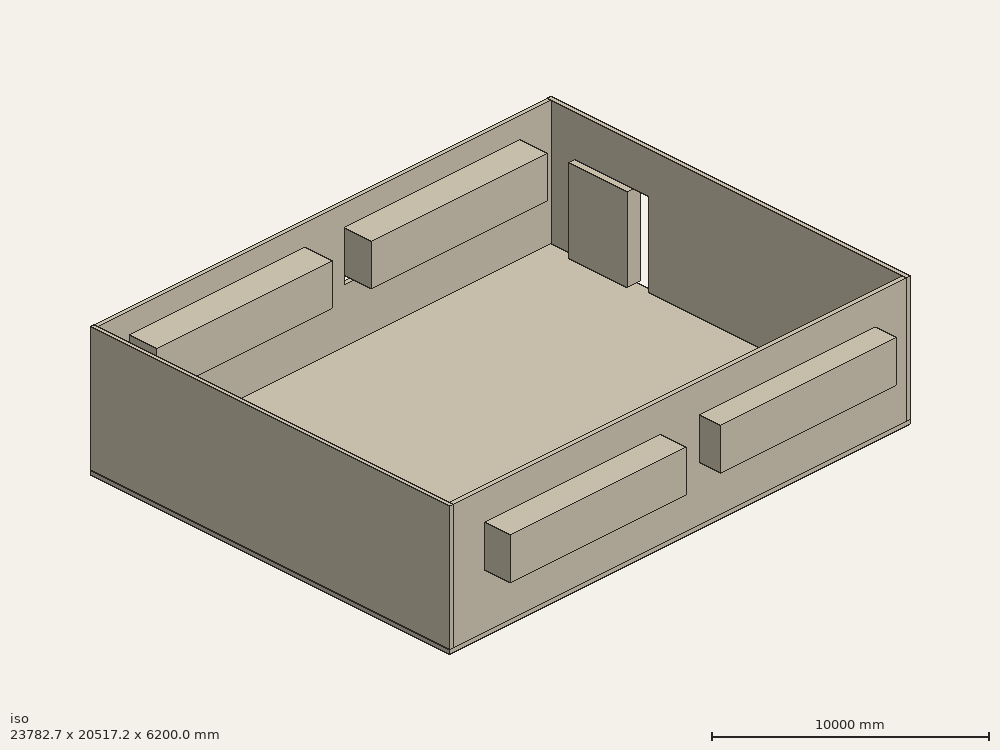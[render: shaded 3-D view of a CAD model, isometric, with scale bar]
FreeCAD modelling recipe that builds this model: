
FCSTD DOCUMENT  (FreeCAD 0.19R)
Label: warehouse
License: All rights reserved
LicenseURL: http://en.wikipedia.org/wiki/All_rights_reserved
objects: App::FeaturePython×14, Part::Box×5, Part::FeaturePython×5, Sketcher::SketchObject×4, App::MaterialObjectPython×2, Part::Part2DObjectPython×1, App::DocumentObjectGroupPython×1, App::DocumentObjectGroup×1, App::GeometryPython×1
note: 16 computed .brp shape members not serialized (recipe doc carries the construction recipe); baked Part::Feature solids carry a one-line shape summary decoded from their .brp

FEATURE [Sketcher::SketchObject] WallTrace002
  FullyConstrained = false
  sketch-geometry (1):
    g0: LineSegment StartX=-1.1328e-12 StartY=18500 StartZ=0 EndX=23200 EndY=18500 EndZ=0
FEATURE [Sketcher::SketchObject] WallTrace
  FullyConstrained = false
  sketch-geometry (1):
    g0: LineSegment StartX=-100 StartY=-200 StartZ=0 EndX=-100 EndY=18200 EndZ=0
FEATURE [Sketcher::SketchObject] WallTrace001
  FullyConstrained = false
  sketch-geometry (1):
    g0: LineSegment StartX=-6.1e-15 StartY=-100 StartZ=0 EndX=23200 EndY=-100 EndZ=0
FEATURE [App::FeaturePython] Dimension001  # Draft dimension (typed FeaturePython)
  Diameter = false
  Dimline = (9000,8000,0)
  Direction = (0,0,0)
  Distance = 23200
  End = (23200,9000,0)
  Normal = (0,0,1)
  Start = (-8.353e-13,9000,0)
FEATURE [App::FeaturePython] Dimension  # Draft dimension (typed FeaturePython)
  Diameter = false
  Dimline = (11900,8900,0)
  Direction = (0,0,0)
  Distance = 18000
  End = (11600,0,0)
  Normal = (0,0,1)
  Start = (11600,18000,0)
FEATURE [Sketcher::SketchObject] WallTrace003
  FullyConstrained = false
  sketch-geometry (1):
    g0: LineSegment StartX=23300 StartY=18600 StartZ=0 EndX=23300 EndY=200 EndZ=0
FEATURE [Part::Box] Cube
  AttacherType = Attacher::AttachEngine3D
  Height = 4000
  Length = 687.6
  Placement = pos=(23582.7,16800,0) rot=(0,0,1;3.14159rad)
  Width = 3000
FEATURE [App::FeaturePython] Dimension002  # Draft dimension (typed FeaturePython)
  Diameter = false
  Dimline = (22729.1,17106.1,0)
  Direction = (0,0,0)
  Distance = 2000
  End = (22682.3,16000,0)
  Normal = (0,0,1)
  Start = (22682.3,18000,0)
FEATURE [App::FeaturePython] Dimension003  # Draft dimension (typed FeaturePython)
  Diameter = false
  Dimline = (23259.5,14201,0)
  Direction = (0,0,0)
  Distance = 3000
  End = (23326.6,13000,0)
  Normal = (0,0,1)
  Start = (23326.6,16000,0)
FEATURE [App::MaterialObjectPython] Material  label="Concrete"  # material (typed FeaturePython)
  Description = A standard C-25 construction concrete
  Material = AuthorAndLicense=Concrete-Generic,CardName=Concrete-Generic,Color=(1.0, 0.7568627450980392, 0.27058823529411763, 1.0),CompressiveStrength=25 MPa,+12 more (map truncated)
  ProductURL = https://en.wikipedia.org/wiki/Concrete
  StandardCode = Masterformat 03 33 13
  Transparency = 0
FEATURE [Part::FeaturePython] Wall003  # Arch/BIM 166 (typed FeaturePython)
  Align = 2
  Area = 0
  Base = -> WallTrace003
  BlockHeight = 0
  BlockLength = 0
  CountBroken = 0
  CountEntire = 0
  Face = 0
  Height = 0
  HorizontalArea = 3680000
  IfcData = attributes={"GlobalId": {"name": "GlobalId", "type": "IfcGloballyUniqueId", "is_enum": false, "enum_values": []}, "Description": {"... (+533 chars omitted),+1 more (map truncated)
  IfcType = 166
  Joint = 0
  Length = 18400
  MakeBlocks = false
  Material = -> Material
  MoveBase = false
  MoveWithHost = false
  Normal = (0,0,1)
  OffsetFirst = 0
  OffsetSecond = 0
  PerimeterLength = 37200
  Placement = pos=(0,-400,0) rot=(0,0,1;0rad)
  PredefinedType = 0
  Subtractions = -> [Cube]
  VerticalArea = 200800000
  Width = 200
FEATURE [Part::FeaturePython] Wall001  # Arch/BIM 166 (typed FeaturePython)
  Align = 2
  Area = 0
  Base = -> WallTrace
  BlockHeight = 0
  BlockLength = 0
  CountBroken = 0
  CountEntire = 0
  Face = 0
  Height = 0
  HorizontalArea = 3.68e+06
  IfcData = attributes={"GlobalId": {"name": "GlobalId", "type": "IfcGloballyUniqueId", "is_enum": false, "enum_values": []}, "Description": {"... (+533 chars omitted),+1 more (map truncated)
  IfcType = 166
  Joint = 0
  Length = 18400
  MakeBlocks = false
  Material = -> Material
  MoveBase = false
  MoveWithHost = false
  Normal = (0,0,1)
  OffsetFirst = 0
  OffsetSecond = 0
  PerimeterLength = 37200
  PredefinedType = 0
  VerticalArea = 223200000
  Width = 200
FEATURE [Part::Part2DObjectPython] Rectangle  # Draft 2D object (typed FeaturePython)
  Area = 434240000
  ChamferSize = 0
  Columns = 1
  FilletRadius = 0
  Height = 18400
  Length = 23600
  MakeFace = true
  Placement = pos=(-200,-200,0) rot=(0,0,1;0rad)
  Rows = 1
FEATURE [App::MaterialObjectPython] Material001  label="Wood"  # material (typed FeaturePython)
  Description = A standard construction wood
  Material = AuthorAndLicense=Wood-Generic,CardName=Wood-Generic,Color=(0.7098039215686275, 0.6274509803921569, 0.5254901960784314, 1.0),Density=700 kg/m^3,+10 more (map truncated)
  ProductURL = https://en.wikipedia.org/wiki/Wood
  Transparency = 0
FEATURE [App::DocumentObjectGroupPython] MaterialContainer  label="Materials"  # scripted group (container) (typed FeaturePython)
  Group = -> [Material,Material001]
FEATURE [Part::FeaturePython] Structure  label="Slab"  # Arch/BIM 118 (typed FeaturePython)
  Base = -> Rectangle
  FaceMaker = 0
  Height = 200
  HorizontalArea = 434240000
  IfcData = attributes={"GlobalId": {"name": "GlobalId", "type": "IfcGloballyUniqueId", "is_enum": false, "enum_values": []}, "Description": {"... (+453 chars omitted),+1 more (map truncated)
  IfcType = 118
  Length = 18400
  Material = -> Material001
  MoveBase = false
  MoveWithHost = false
  Nodes = (4) [(-200,-200,0),(23400,-200,0),(23400,18200,0),(-200,18200,0)]
  NodesOffset = 0
  Normal = (0,0,-1)
  PerimeterLength = 84000
  PredefinedType = 0
  VerticalArea = 16800000
  Width = 23600
FEATURE [Part::Box] Cube001
  AttacherType = Attacher::AttachEngine3D
  Height = 2400
  Length = 9000
  Placement = pos=(1600,16600,5000) rot=(-1,0,0;1.5708rad)
  Width = 2000
FEATURE [Part::Box] Cube002
  AttacherType = Attacher::AttachEngine3D
  Height = 2400
  Length = 9000
  Placement = pos=(12600,16600,5000) rot=(-1,0,0;1.5708rad)
  Width = 2000
FEATURE [Part::FeaturePython] Wall002  # Arch/BIM 166 (typed FeaturePython)
  Align = 2
  Area = 0
  Base = -> WallTrace002
  BlockHeight = 0
  BlockLength = 0
  CountBroken = 0
  CountEntire = 0
  Face = 0
  Height = 0
  HorizontalArea = 8240000
  IfcData = attributes={"GlobalId": {"name": "GlobalId", "type": "IfcGloballyUniqueId", "is_enum": false, "enum_values": []}, "Description": {"... (+533 chars omitted),+1 more (map truncated)
  IfcType = 166
  Joint = 0
  Length = 23200
  MakeBlocks = false
  Material = -> Material
  MoveBase = false
  MoveWithHost = false
  Normal = (0,0,1)
  OffsetFirst = 0
  OffsetSecond = 0
  PerimeterLength = 46800
  Placement = pos=(0,-400,0) rot=(0,0,1;0rad)
  PredefinedType = 0
  Subtractions = -> [Cube001,Cube002]
  VerticalArea = 210400000
  Width = 200
FEATURE [App::FeaturePython] Dimension004  # Draft dimension (typed FeaturePython)
  Diameter = false
  Dimline = (5543.57,18000,5245.84)
  Direction = (0,0,0)
  Distance = 1400
  End = (5339.7,18000,6000)
  Normal = (0,-1,-2e-16)
  Start = (5339.7,18000,4600)
FEATURE [App::FeaturePython] Dimension005  # Draft dimension (typed FeaturePython)
  Diameter = false
  Dimline = (15947.4,18000,5378.28)
  Direction = (0,0,0)
  Distance = 1400
  End = (15674.9,18000,6000)
  Normal = (0,-1,-2e-16)
  Start = (15674.9,18000,4600)
FEATURE [App::FeaturePython] Dimension007  # Draft dimension (typed FeaturePython)
  Diameter = false
  Dimline = (22484.2,18000,3327.9)
  Direction = (0,0,0)
  Distance = 1600
  End = (23200,18000,3606.66)
  Normal = (0,-1,-2e-16)
  Start = (21600,18000,3606.66)
FEATURE [App::FeaturePython] Dimension008  # Draft dimension (typed FeaturePython)
  Diameter = false
  Dimline = (807.933,18000,3641.47)
  Direction = (0,0,0)
  Distance = 1600
  End = (1600,17782.2,3742.82)
  Normal = (0,-1,-2e-16)
  Start = (7.276e-12,17782.2,3742.82)
FEATURE [Part::Box] Cube003
  AttacherType = Attacher::AttachEngine3D
  Height = 2400
  Length = 9000
  Placement = pos=(1600,-1517.2,4600) rot=(-1,0,0;1.5708rad)
  Width = 2000
FEATURE [Part::Box] Cube004
  AttacherType = Attacher::AttachEngine3D
  Height = 2400
  Length = 9000
  Placement = pos=(12600,-1281.2,4600) rot=(-1,0,0;1.5708rad)
  Width = 2000
FEATURE [Part::FeaturePython] Wall  # Arch/BIM 166 (typed FeaturePython)
  Align = 2
  Area = 0
  Base = -> WallTrace001
  BlockHeight = 0
  BlockLength = 0
  CountBroken = 0
  CountEntire = 0
  Face = 0
  Height = 0
  HorizontalArea = 8240000
  IfcData = attributes={"GlobalId": {"name": "GlobalId", "type": "IfcGloballyUniqueId", "is_enum": false, "enum_values": []}, "Description": {"... (+533 chars omitted),+1 more (map truncated)
  IfcType = 166
  Joint = 0
  Length = 23200
  MakeBlocks = false
  Material = -> Material
  MoveBase = false
  MoveWithHost = false
  Normal = (0,0,1)
  OffsetFirst = 0
  OffsetSecond = 0
  PerimeterLength = 46800
  PredefinedType = 0
  Subtractions = -> [Cube004,Cube003]
  VerticalArea = 210400000
  Width = 200
FEATURE [App::FeaturePython] Dimension009  # Draft dimension (typed FeaturePython)
  Diameter = false
  Dimline = (22414.3,-3.638e-12,4033.04)
  Direction = (0,0,0)
  Distance = 1600
  End = (21600,374.029,3928.31)
  Normal = (-1e-16,1,0)
  Start = (23200,374.029,3928.31)
FEATURE [App::FeaturePython] Dimension010  # Draft dimension (typed FeaturePython)
  Diameter = false
  Dimline = (845.934,-3.638e-12,4347.79)
  Direction = (0,0,0)
  Distance = 1600
  End = (2.274e-13,-9.41e-14,3906)
  Normal = (-1e-16,1,0)
  Start = (1600,0,3906)
FEATURE [App::FeaturePython] Dimension011  # Draft dimension (typed FeaturePython)
  Diameter = false
  Dimline = (14945.2,-3.638e-12,5192.81)
  Direction = (0,0,0)
  Distance = 1400
  End = (15741.5,9.202e-13,6000)
  Normal = (-1e-16,1,0)
  Start = (15741.5,9.202e-13,4600)
FEATURE [App::FeaturePython] Dimension012  # Draft dimension (typed FeaturePython)
  Diameter = false
  Dimline = (5139.33,0,5233.23)
  Direction = (0,0,0)
  Distance = 1400
  End = (5456.04,2.923e-13,6000)
  Normal = (-1e-16,1,0)
  Start = (5456.04,2.923e-13,4600)
FEATURE [App::FeaturePython] Dimension013  # Draft dimension (typed FeaturePython)
  Diameter = false
  Dimline = (7182.36,4.223e-13,3691.36)
  Direction = (0,0,0)
  Distance = 2000
  End = (7098.11,-49.4492,4600)
  Normal = (-1e-16,1,0)
  Start = (7098.11,-49.4492,2600)
FEATURE [App::FeaturePython] Dimension014  # Draft dimension (typed FeaturePython)
  Diameter = false
  Dimline = (7600,18000,3290.7)
  Direction = (0,0,0)
  Distance = 2000
  End = (7821.38,18000,4600)
  Normal = (0,-1,0)
  Start = (7821.38,18000,2600)
FEATURE [App::DocumentObjectGroup] Group  label="Annotations"
  Group = -> [Dimension003,Dimension002,Dimension,Dimension001,Dimension004,Dimension005,Dimension007,Dimension008,Dimension010,Dimension009,Dimension011,Dimension012,Dimension013,Dimension014]
FEATURE [App::GeometryPython] BuildingPart  label="Floor"  # Arch/BIM 14 (typed FeaturePython)
  Area = 0
  CompositionType = 0
  Elevation = 0
  Group = -> [Wall,Wall001,Wall002,Wall003,Group,Structure]
  Height = 6000
  HeightPropagate = true
  IfcData = attributes={"GlobalId": {"name": "GlobalId", "type": "IfcGloballyUniqueId", "is_enum": false, "enum_values": []}, "Description": {"... (+880 chars omitted),+1 more (map truncated)
  IfcType = 14
  LevelOffset = 0
  LongName = Floor
  expr: Elevation = .Placement.Base.z
